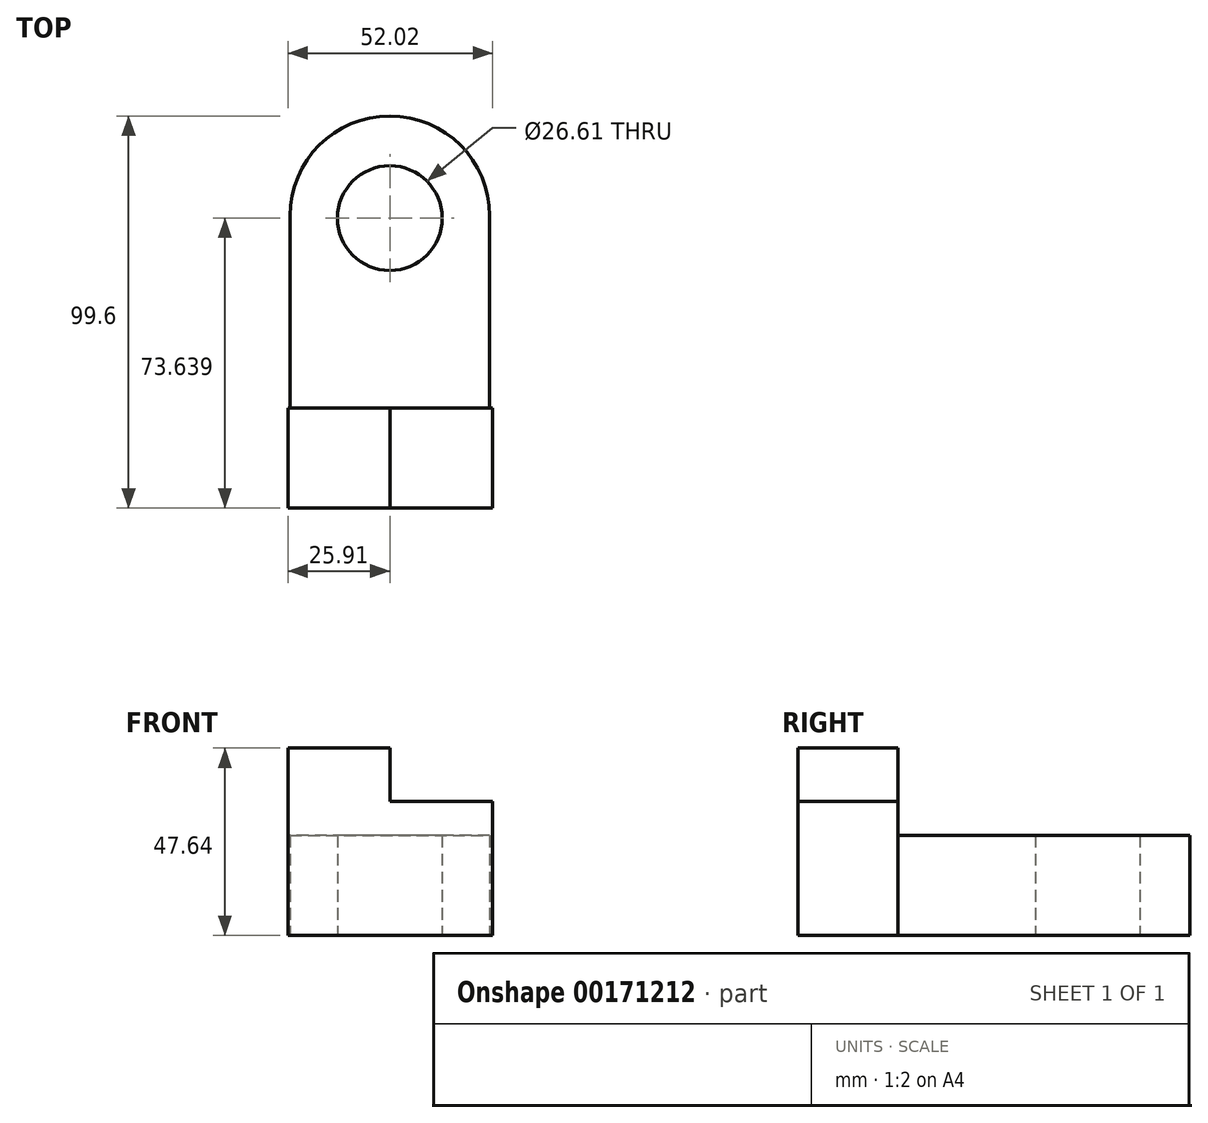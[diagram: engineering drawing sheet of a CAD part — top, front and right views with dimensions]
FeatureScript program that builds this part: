
annotation { "Feature Type Name" : "Feature", "Feature Type Description" : "" }
export const myFeature = defineFeature(function(context is Context, id is Id, definition is map)
    precondition{}
    {
        {
            var Q0;
            Q0=qCreatedBy(makeId("Top.planeOp"),FACE);
            var sketch = newSketch(context, id + "F0", { "sketchPlane" : qUnion([Q0])});
            skCircle(sketch, "E0", {"center": v(0, 48.83) * mm, "radius": 25.37 * mm});
            skLineSegment(sketch, "E1.bottom", {"start": v(-25.37, 48.83) * mm, "end": v(25.37, 48.83) * mm});
            skLineSegment(sketch, "E1.top", {"start": v(-25.37, 0) * mm, "end": v(25.37, 0) * mm});
            skLineSegment(sketch, "E1.left", {"start": v(-25.37, 48.83) * mm, "end": v(-25.37, 0) * mm});
            skLineSegment(sketch, "E1.right", {"start": v(25.37, 48.83) * mm, "end": v(25.37, 0) * mm});
            skSolve(sketch);
        }
        {
            var Q0;
            Q0 = qSketchRegion(id + "F0", true);
            extrude(context, id + "F1", {"entities" : qUnion([Q0]), "depth" : 25.4 * mm});
        }
        {
            var Q0;
            Q0=qCreatedBy(makeId("Top.planeOp"),FACE);
            var sketch = newSketch(context, id + "F2", { "sketchPlane" : qUnion([Q0])});
            skCircle(sketch, "E2", {"center": v(0, 48.24) * mm, "radius": 13.3 * mm});
            skSolve(sketch);
        }
        {
            var Q0;
            Q0=makeQuery(id+"F2.imprint","IMPRINT",FACE,{"disambiguationData":[TD([[makeQuery(id+"F2.imprint","IMPRINT",EDGE,{"derivedFrom":sQuery(id+"F2.wireOp",EDGE,"E2")}),1.0]])]});
            var Q1;
            Q1=sQuery(id+"F2.wireOp",EDGE,"E2");
            extrude(context, id + "F3", {"entities" : qUnion([Q0]), "operationType" : NewBodyOperationType.REMOVE, "surfaceEntities" : qUnion([Q1]), "endBound" : BoundingType.THROUGH_ALL, "depth" : 25.4 * mm});
        }
        {
            var Q0;
            Q0=makeQuery(id+"F2.imprint","IMPRINT",FACE,{"disambiguationData":[TD([[makeQuery(id+"F2.imprint","IMPRINT",EDGE,{"derivedFrom":sQuery(id+"F2.wireOp",EDGE,"E2")}),1.0]])]});
            var sketch = newSketch(context, id + "F4", { "sketchPlane" : qUnion([Q0])});
            skSolve(sketch);
        }
        {
            var Q0;
            Q0 = qSketchRegion(id + "F4", true);
            var Q1;
            Q1=makeQuery(id+"F2.imprint","IMPRINT",FACE,{"disambiguationData":[TD([[makeQuery(id+"F2.imprint","IMPRINT",EDGE,{"derivedFrom":sQuery(id+"F2.wireOp",EDGE,"E2")}),1.0]])]});
            extrude(context, id + "F5", {"entities" : qUnion([Q0, Q1]), "operationType" : NewBodyOperationType.REMOVE, "endBound" : BoundingType.THROUGH_ALL, "depth" : 25.4 * mm});
        }
        {
            var Q0;
            Q0=qCreatedBy(makeId("Front.planeOp"),FACE);
            var sketch = newSketch(context, id + "F6", { "sketchPlane" : qUnion([Q0])});
            skLineSegment(sketch, "E3.bottom", {"start": v(-25.9, 47.64) * mm, "end": v(26.11, 47.64) * mm});
            skLineSegment(sketch, "E3.top", {"start": v(-25.9, 0) * mm, "end": v(26.11, 0) * mm});
            skLineSegment(sketch, "E3.left", {"start": v(-25.9, 47.64) * mm, "end": v(-25.9, 0) * mm});
            skLineSegment(sketch, "E3.right", {"start": v(26.11, 47.64) * mm, "end": v(26.11, 0) * mm});
            skSolve(sketch);
        }
        {
            var Q0;
            Q0=makeQuery(id+"F6.imprint","IMPRINT",FACE,{"disambiguationData":[TD([[makeQuery(id+"F6.imprint","IMPRINT",EDGE,{"derivedFrom":sQuery(id+"F6.wireOp",EDGE,"E3.bottom")}),-1.0]])]});
            extrude(context, id + "F7", {"entities" : qUnion([Q0]), "operationType" : NewBodyOperationType.ADD, "depth" : 25.4 * mm});
        }
        {
            var Q0;
            Q0=qCreatedBy(makeId("Front.planeOp"),FACE);
            var sketch = newSketch(context, id + "F8", { "sketchPlane" : qUnion([Q0])});
            skLineSegment(sketch, "E4.bottom", {"start": v(0, 48.45) * mm, "end": v(26.2, 48.45) * mm});
            skLineSegment(sketch, "E4.top", {"start": v(0, 34.1) * mm, "end": v(26.2, 34.1) * mm});
            skLineSegment(sketch, "E4.left", {"start": v(0, 48.45) * mm, "end": v(0, 34.1) * mm});
            skLineSegment(sketch, "E4.right", {"start": v(26.2, 48.45) * mm, "end": v(26.2, 34.1) * mm});
            skSolve(sketch);
        }
        {
            var Q0;
            Q0 = qSketchRegion(id + "F8", true);
            extrude(context, id + "F9", {"entities" : qUnion([Q0]), "operationType" : NewBodyOperationType.REMOVE, "depth" : 25.4 * mm});
        }
    });
